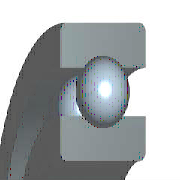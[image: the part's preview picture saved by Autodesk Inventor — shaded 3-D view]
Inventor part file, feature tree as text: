
AUTODESK INVENTOR PART (.ipt)
format: ipt  version: 2015 (Build 190159000, 159)  size: 345,600 bytes
history: native  units: mm (DEFAULTED — no unit token found)
features: sketch x5, other x3, plane x2, pattern_circular x1, fillet x1
ambient origin geometry x8: Origin, YZ Plane, XZ Plane, XY Plane, X Axis, Y Axis, Z Axis, Center Point
bodies: Solid1 (feature_tree)
feature tree (12):
  sketch  "Sketch1"  dims[d2=72.0mm]
  other  "WorkPoint1"
  other  "WorkAxis1"
  plane  "WorkPlane3"
  plane  "WorkPlane4"
  sketch  "Sketch4"  dims[d5=4.0mm]
  other  "WorkPoint2"
  pattern_circular  "PolarArray1"  Count=2  [1 undecoded]
  fillet  "Fillet1"  Radius=3.0mm
  sketch  "Sketch2"  dims[d3=10.0mm]
  sketch  "Sketch3"  dims[d4=19.0mm]
  sketch  "Sketch5"  dims[d6=360.0deg d7=0.0mm d8=15.6mm d9=2.1mm d10=360.0deg d11=-4.0mm d12=0.0mm d13=0.0mm d14=15.6001mm d15=2.1001mm d16=360.0deg d17=50.428571mm d19=360.0deg d20=0.15mm d21=2.62mm d22=3.25mm d23=3.88mm d26=0.0mm d27=0.0mm d28=0.0mm d29=0.0mm d30=0.0mm]
note: 1 required parameter value undecoded (feature->parameter linkage not recoverable at this tier; creation-order binding heuristic only, values carry confidence <= 0.55)
